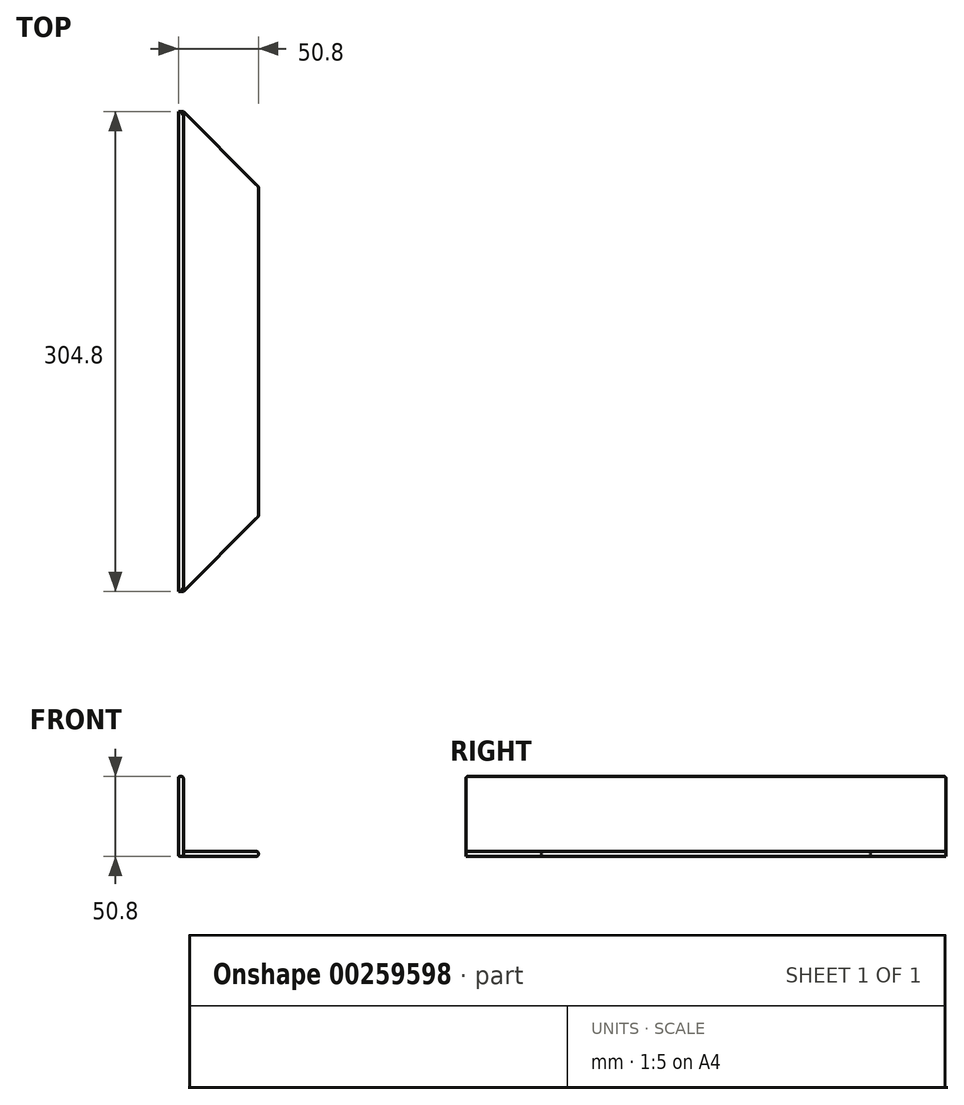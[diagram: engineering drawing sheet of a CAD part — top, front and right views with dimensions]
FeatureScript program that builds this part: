
annotation { "Feature Type Name" : "Feature", "Feature Type Description" : "" }
export const myFeature = defineFeature(function(context is Context, id is Id, definition is map)
    precondition{}
    {
        {
            var Q0;
            Q0=qCreatedBy(makeId("Front.planeOp"),FACE);
            var sketch = newSketch(context, id + "F0", { "sketchPlane" : qUnion([Q0])});
            skLineSegment(sketch, "E0", {"start": v(0, 0) * mm, "end": v(0, 50.8) * mm});
            skLineSegment(sketch, "E1", {"start": v(0, 50.8) * mm, "end": v(3.17, 50.8) * mm});
            skLineSegment(sketch, "E2", {"start": v(3.17, 50.8) * mm, "end": v(3.18, 3.17) * mm});
            skLineSegment(sketch, "E3", {"start": v(3.18, 3.17) * mm, "end": v(50.8, 3.18) * mm});
            skLineSegment(sketch, "E4", {"start": v(50.8, 3.18) * mm, "end": v(50.8, 0) * mm});
            skLineSegment(sketch, "E5", {"start": v(50.8, 0) * mm, "end": v(0, 0) * mm});
            skSolve(sketch);
        }
        {
            var Q0;
            Q0=makeQuery(id+"F0.imprint","IMPRINT",FACE,{"disambiguationData":[TD([[makeQuery(id+"F0.imprint","IMPRINT",EDGE,{"derivedFrom":sQuery(id+"F0.wireOp",EDGE,"E0")}),-1.0]])]});
            extrude(context, id + "F1", {"entities" : qUnion([Q0]), "depth" : 304.8 * mm, "symmetric" : true});
        }
        {
            var Q0;
            Q0=makeQuery(id+"F1.opExtrude","SWEPT_FACE",FACE,{"disambiguationData":[OSD([sQuery(id+"F0.wireOp",EDGE,"E3")])]});
            var sketch = newSketch(context, id + "F2", { "sketchPlane" : qUnion([Q0])});
            skLineSegment(sketch, "E6", {"start": v(3.18, 152.4) * mm, "end": v(50.8, 104.78) * mm});
            skSolve(sketch);
        }
        {
            var Q0;
            Q0=makeQuery(id+"F1.opExtrude","SWEPT_FACE",FACE,{"disambiguationData":[OSD([sQuery(id+"F0.wireOp",EDGE,"E1")])]});
            fillet(context, id + "F3", {"entities" : qUnion([Q0]), "radius" : 1.27 * mm, "tangentPropagation" : true, "allowEdgeOverflow" : false});
        }
        {
            var Q0;
            {var subQ0=sQuery(id+"F2.wireOp",EDGE,"E6");Q0=makeQuery(id+"F2.imprint","IMPRINT",FACE,{"disambiguationData":[TD([[makeQuery(id+"F2.imprint","IMPRINT",EDGE,{"derivedFrom":subQ0}),1.0]])]});}
            extrude(context, id + "F4", {"entities" : qUnion([Q0]), "operationType" : NewBodyOperationType.REMOVE, "oppositeDirection" : true, "depth" : 3.8 * mm});
        }
        {
            var Q0;
            Q0=makeQuery(id+"F1.opExtrude","SWEPT_FACE",FACE,{"disambiguationData":[OSD([sQuery(id+"F0.wireOp",EDGE,"E3")])]});
            var sketch = newSketch(context, id + "F5", { "sketchPlane" : qUnion([Q0])});
            skLineSegment(sketch, "E7", {"start": v(3.17, -152.4) * mm, "end": v(50.8, -104.77) * mm});
            skSolve(sketch);
        }
        {
            var Q0;
            {var subQ0=sQuery(id+"F5.wireOp",EDGE,"E7");Q0=makeQuery(id+"F5.imprint","IMPRINT",FACE,{"disambiguationData":[TD([[makeQuery(id+"F5.imprint","IMPRINT",EDGE,{"derivedFrom":subQ0}),-1.0]])]});}
            extrude(context, id + "F6", {"entities" : qUnion([Q0]), "operationType" : NewBodyOperationType.REMOVE, "oppositeDirection" : true, "depth" : 3.8 * mm});
        }
        {
            var Q0;
            Q0=makeQuery(id+"F1.opExtrude","SWEPT_FACE",FACE,{"disambiguationData":[OSD([sQuery(id+"F0.wireOp",EDGE,"E4")])]});
            fillet(context, id + "F7", {"entities" : qUnion([Q0]), "radius" : 1.27 * mm, "tangentPropagation" : true, "allowEdgeOverflow" : false});
        }
        {
            var Q0;
            Q0=makeQuery(id+"F1.opExtrude","SWEPT_EDGE",EDGE,{"disambiguationData":[OSD([sQuery(id+"F0.wireOp",EDGE,"E0"),sQuery(id+"F0.wireOp",EDGE,"E5")])]});
            fillet(context, id + "F8", {"entities" : qUnion([Q0]), "radius" : 1.27 * mm, "tangentPropagation" : true, "allowEdgeOverflow" : false});
        }
    });
